# Revit family: 117-DISPENSADOR DE JABÓN LÍQUIDO 1.2 L AC INOX
name_source: partatom
category: Aparatos sanitarios
units: mm (PartAtom-declared; Revit-internal decimal feet)

## family parameters
Anfitrión = Muro
Compartido = Sí
Corte con vacíos al cargar = Sí
Cota de conector redondo = Diámetro de uso
Número OmniClass = 23.45.00.00
Punto de cálculo de habitación = No
Siempre vertical = Sí
Tipo de pieza = Normal
Título OmniClass = Sanitary, Laundry, and Cleaning Equipment

## types (1)
- DISPENSADOR DE JABÓN LÍQUIDO 1.2 L AC INOX
    Elevación por defecto = 900 mm
    F_Alto = 202 mm
    F_Ancho = 123 mm
    F_Color = Acero inoxidable ss304 brillante
    F_Consumo / Capacidad de agua (L) = 1.2
    F_Descripción = Dispensador de jabón liquido vertical con depósito de polietileno, accionado por pulsador manual, apto para jabón líquido, crema y bloqueador solar
    F_Peso = 0 kgf
    F_Productos incluidos = Set de fijación y llave de seguridad
    F_Profundidad = 76 mm
    F_SKU = SAI025853101CB
    F_Tipo de instalación = A muro
    F_Tolerancia dimensional = '+- 5%
    URL = https://briggs.cl
    shaft = No
